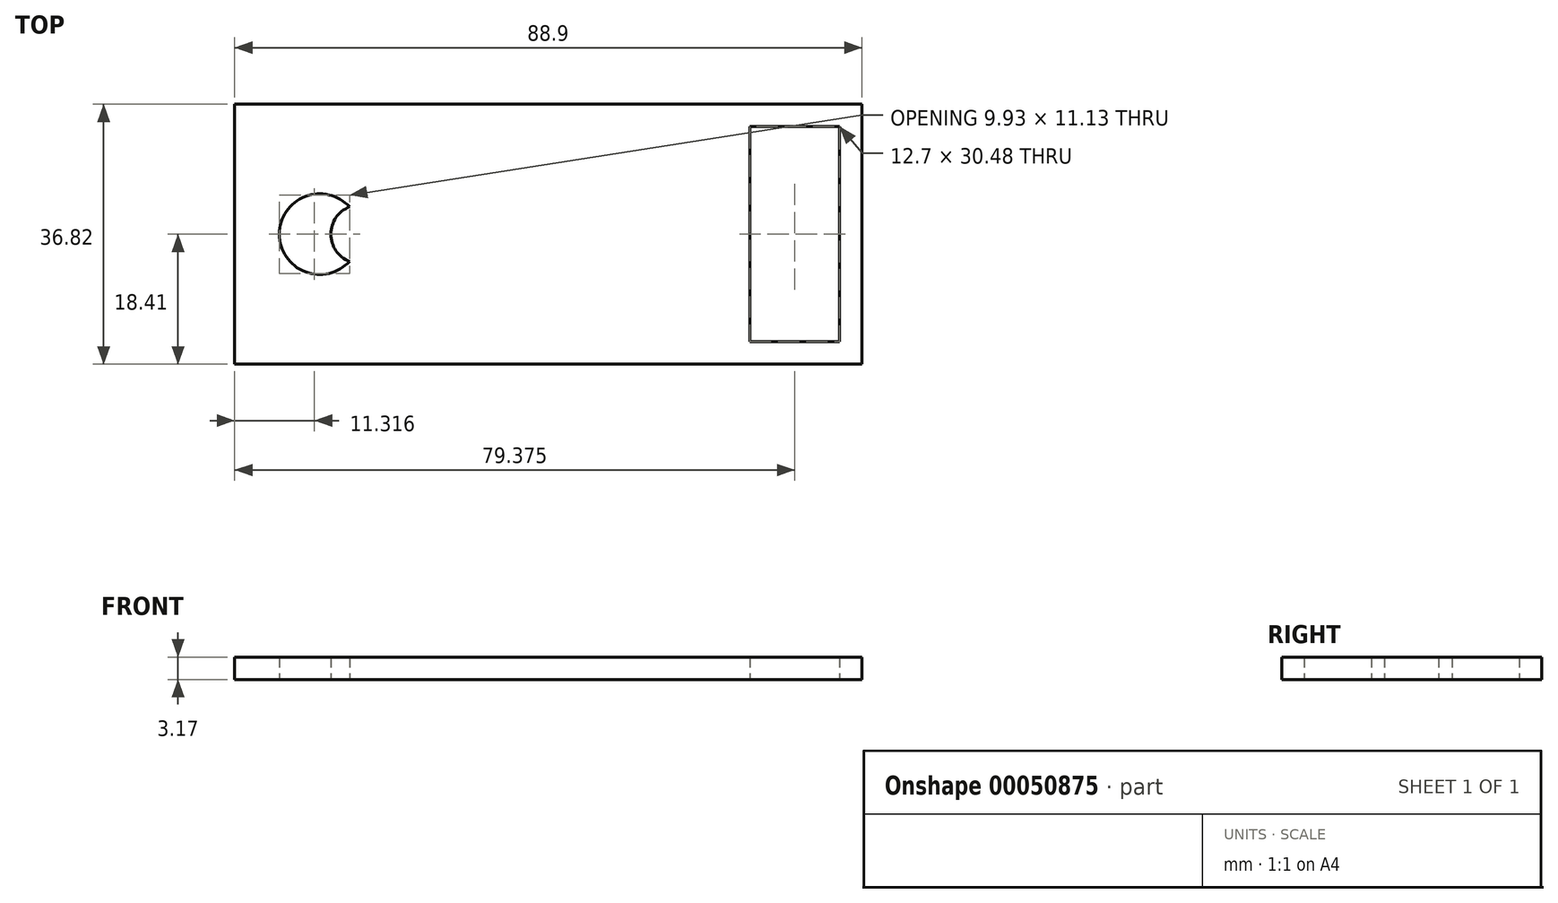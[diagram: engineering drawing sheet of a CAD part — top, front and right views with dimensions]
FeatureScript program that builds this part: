
annotation { "Feature Type Name" : "Feature", "Feature Type Description" : "" }
export const myFeature = defineFeature(function(context is Context, id is Id, definition is map)
    precondition{}
    {
        {
            var Q0;
            Q0=qCreatedBy(makeId("Top.planeOp"),FACE);
            var sketch = newSketch(context, id + "F0", { "sketchPlane" : qUnion([Q0])});
            skLineSegment(sketch, "E0.rect.bottom", {"start": v(44.45, 18.41) * mm, "end": v(-44.45, 18.42) * mm});
            skLineSegment(sketch, "E0.rect.top", {"start": v(44.45, -18.42) * mm, "end": v(-44.45, -18.41) * mm});
            skLineSegment(sketch, "E0.rect.left", {"start": v(44.45, 18.42) * mm, "end": v(44.45, -18.42) * mm});
            skLineSegment(sketch, "E0.rect.right", {"start": v(-44.45, 18.41) * mm, "end": v(-44.45, -18.41) * mm});
            skPoint(sketch, "E0.rect.middle", {"position": v(0, 0) * mm});
            skLineSegment(sketch, "E1.bottom", {"start": v(41.28, 15.24) * mm, "end": v(28.58, 15.24) * mm});
            skLineSegment(sketch, "E1.top", {"start": v(41.27, -15.24) * mm, "end": v(28.57, -15.24) * mm});
            skLineSegment(sketch, "E1.left", {"start": v(41.28, 15.24) * mm, "end": v(41.27, -15.24) * mm});
            skLineSegment(sketch, "E1.right", {"start": v(28.58, 15.24) * mm, "end": v(28.57, -15.24) * mm});
            skArc(sketch, "E2", {"start": v(-28.17, 3.86) * mm, "mid": v(-38.1, 0) * mm, "end": v(-28.17, -3.86) * mm});
            skArc(sketch, "E3", {"start": v(-28.17, 3.86) * mm, "mid": v(-30.8, 0) * mm, "end": v(-28.17, -3.86) * mm});
            skPoint(sketch, "E4", {"position": v(-28.17, 3.86) * mm});
            skPoint(sketch, "E5", {"position": v(-28.17, -3.86) * mm});
            skLineSegment(sketch, "E6", {"start": v(0, 0) * mm, "end": v(-44.45, 0) * mm, "construction": true});
            skSolve(sketch);
        }
        {
            var Q0;
            Q0=makeQuery(id+"F0.imprint","IMPRINT",FACE,{"disambiguationData":[TD([[makeQuery(id+"F0.imprint","IMPRINT",EDGE,{"derivedFrom":sQuery(id+"F0.wireOp",EDGE,"E0.rect.bottom")}),1.0]])]});
            extrude(context, id + "F1", {"entities" : qUnion([Q0]), "depth" : 3.17 * mm});
        }
    });
